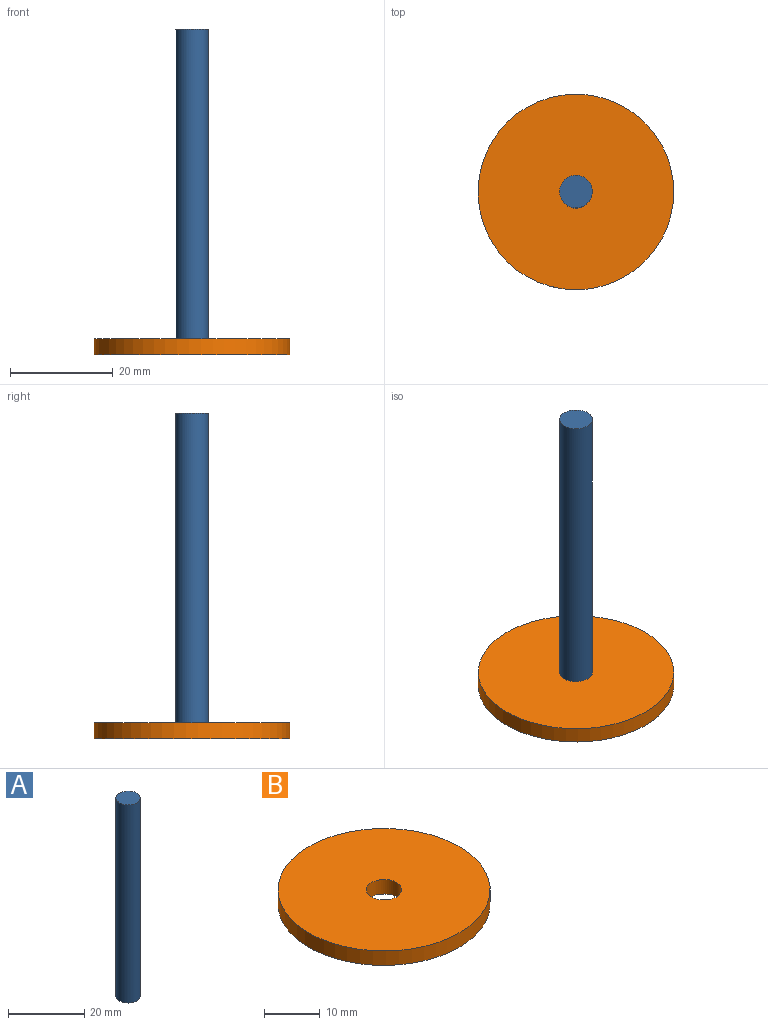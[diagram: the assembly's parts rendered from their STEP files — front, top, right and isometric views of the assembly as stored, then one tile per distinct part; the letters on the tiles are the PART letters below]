
ASSEMBLY  parts=2 mates=1
PART A: 3 faces, bbox 6.4x6.4x63.5 mm
  f0: plane 6.35x6.35mm, normal (0,0,1), area 31.7mm2, adj f1
  f1: cylinder r=3.17mm len=63.5mm, axis (0,0,-1), area 1266.8mm2, adj f0,f2
  f2: plane 6.35x6.35mm, normal (0,0,-1), area 31.7mm2, adj f1
PART B: 4 faces, bbox 38.1x38.1x3.2 mm
  f0: cylinder r=3.17mm len=6.35mm, axis (0,0,-1), area 63.3mm2, adj f2,f3
  f1: cylinder r=19.05mm len=38.1mm, axis (0,0,-1), area 380mm2, adj f2,f3
  f2: plane 38.1x38.1mm, normal (0,0,1), area 1108.4mm2, adj f0,f1
  f3: plane 38.1x38.1mm, normal (0,0,-1), area 1108.4mm2, adj f0,f1
PLACE A t=(69.85,0,-69.85)mm
PLACE B t=(69.85,0,-69.85)mm
MATE fastened A.f1 <-> B.f1  axis (0,0,-1) through (0,0,0)mm
